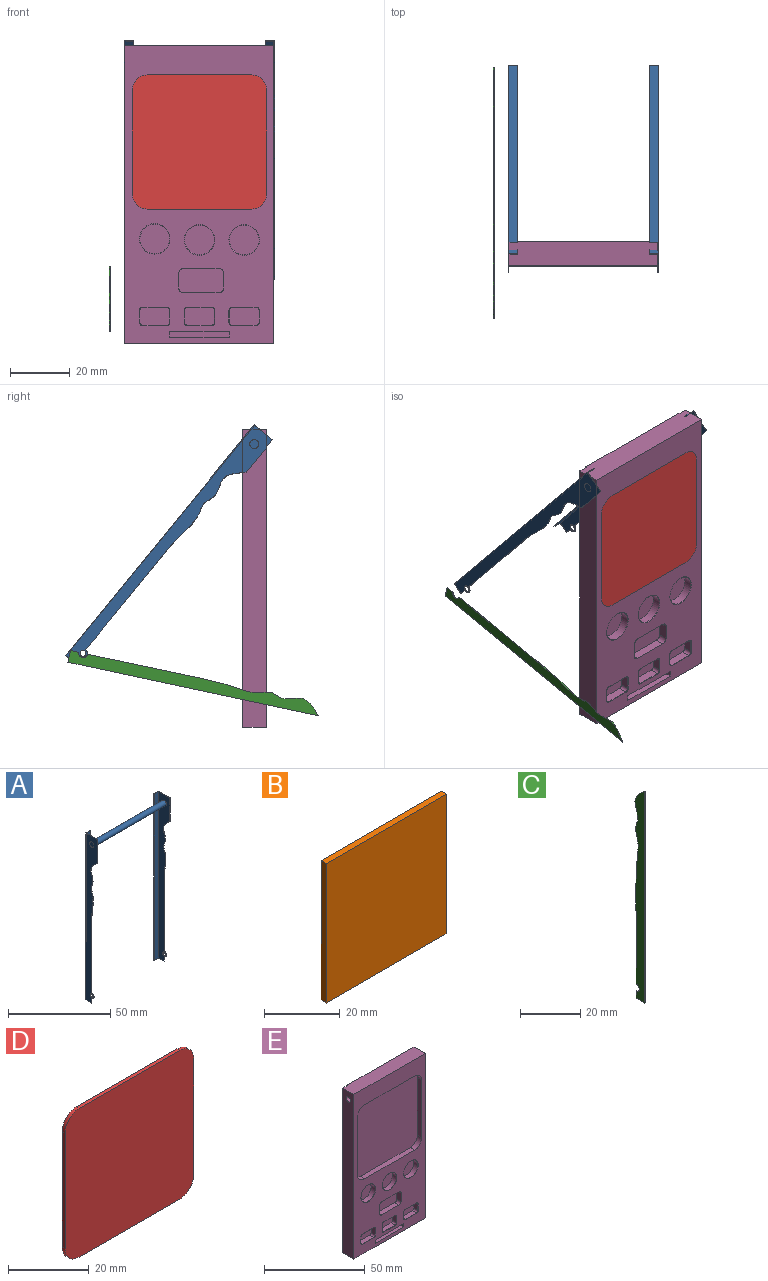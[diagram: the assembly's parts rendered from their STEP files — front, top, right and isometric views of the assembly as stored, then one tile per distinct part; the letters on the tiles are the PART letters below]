
ASSEMBLY  parts=5 mates=9
PART A: 27 faces, bbox 50.4x8x100 mm
  f0: plane 8.17x0.2mm, normal (0,-1,0), area 1.6mm2, adj f6,f8,f20,f25
  f1: plane 2.8x0.2mm, normal (0,-1,0), area 0.6mm2, adj f2,f4,f5,f23
  f2: plane 100x8mm, normal (-1,0,0), area 470.7mm2, adj f1,f3,f5,f11,f13,f21,f22,f23
  f3: plane 14.09x0.2mm, normal (0,-1,0), area 2.8mm2, adj f2,f4,f13,f21
  f4: plane 100x7.8mm, normal (1,0,0), area 443.7mm2, adj f1,f3,f5,f12,f13,f18,f21,f22
  f5: plane 4x3.2mm, normal (0,0,-1), area 1.4mm2, adj f1,f2,f4,f10,f11,f12
  f6: plane 100x7.8mm, normal (-1,0,0), area 443.7mm2, adj f0,f7,f9,f16,f17,f18,f19,f20
  f7: plane 14.09x0.2mm, normal (0,-1,0), area 2.8mm2, adj f6,f8,f17,f20
  f8: plane 100x8mm, normal (1,0,0), area 470.7mm2, adj f0,f7,f9,f14,f17,f19,f20,f25
  f9: plane 4x3.2mm, normal (0,0,-1), area 1.4mm2, adj f6,f8,f14,f15,f16,f19
  f10: plane 100x0.2mm, normal (1,0,0), area 20mm2, adj f5,f11,f12,f13
  f11: plane 100x3.2mm, normal (0,1,0), area 320mm2, adj f2,f5,f10,f13
  f12: plane 100x3mm, normal (0,-1,0), area 300mm2, adj f4,f5,f10,f13
  f13: plane 8x3.2mm, normal (0,0,1), area 2.2mm2, adj f2,f3,f4,f10,f11,f12
  f14: plane 100x3.2mm, normal (0,1,0), area 320mm2, adj f8,f9,f15,f17
  f15: plane 100x0.2mm, normal (-1,0,0), area 20mm2, adj f9,f14,f16,f17
  f16: plane 100x3mm, normal (0,-1,0), area 300mm2, adj f6,f9,f15,f17
  f17: plane 8x3.2mm, normal (0,0,1), area 2.2mm2, adj f6,f7,f8,f14,f15,f16
  f18: cylinder r=1.5mm len=50mm, axis (-1,0,0), area 471.2mm2, adj f4,f6
  f19: plane 2.8x0.2mm, normal (0,-1,0), area 0.6mm2, adj f6,f8,f9,f25
  f20: extruded ~71.94x4.46mm, area 14.8mm2, adj f0,f6,f7,f8
  f21: extruded ~71.94x4.46mm, area 14.8mm2, adj f2,f3,f4,f22
  f22: plane 8.17x0.2mm, normal (0,-1,0), area 1.6mm2, adj f2,f4,f21,f23
  f23: cylinder r=1.5mm len=3mm, axis (-1,0,0), area 0.9mm2, adj f1,f2,f4,f22
  f24: cylinder r=1mm len=2mm, axis (-1,0,0), area 1.3mm2, adj f2,f4
  f25: cylinder r=1.5mm len=3mm, axis (1,0,0), area 0.9mm2, adj f0,f6,f8,f19
  f26: cylinder r=1mm len=2mm, axis (1,0,0), area 1.3mm2, adj f6,f8
PART B: 6 faces, bbox 45x2x45 mm
  f0: plane 45x2mm, normal (0,0,1), area 90mm2, adj f1,f3,f4,f5
  f1: plane 45x2mm, normal (-1,0,0), area 90mm2, adj f0,f2,f4,f5
  f2: plane 45x2mm, normal (0,0,-1), area 90mm2, adj f1,f3,f4,f5
  f3: plane 45x2mm, normal (1,0,0), area 90mm2, adj f0,f2,f4,f5
  f4: plane 45x45mm, normal (0,-1,0), area 2025mm2, adj f0,f1,f2,f3
  f5: plane 45x45mm, normal (0,1,0), area 2025mm2, adj f0,f1,f2,f3
PART C: 8 faces, bbox 0.2x6.2x85.9 mm
  f0: plane 8.17x0.2mm, normal (0,1,0), area 1.6mm2, adj f2,f4,f5,f7
  f1: plane 4x0.2mm, normal (0,0,-1), area 0.8mm2, adj f2,f3,f4,f6
  f2: plane 85.91x6.23mm, normal (1,0,0), area 326.1mm2, adj f0,f1,f3,f5,f6,f7
  f3: plane 85.91x0.2mm, normal (0,-1,0), area 17.2mm2, adj f1,f2,f4,f5
  f4: plane 85.91x6.23mm, normal (-1,0,0), area 326.1mm2, adj f0,f1,f3,f5,f6,f7
  f5: extruded ~71.94x4.46mm, area 14.8mm2, adj f0,f2,f3,f4
  f6: plane 2.8x0.2mm, normal (0,1,0), area 0.6mm2, adj f1,f2,f4,f7
  f7: cylinder r=1.5mm len=3mm, axis (-1,0,0), area 0.9mm2, adj f0,f2,f4,f6
PART D: 10 faces, bbox 45x1x45 mm
  f0: plane 35x1mm, normal (0,0,1), area 35mm2, adj f4,f5,f6,f9
  f1: plane 35x1mm, normal (-1,0,0), area 35mm2, adj f4,f5,f6,f7
  f2: plane 35x1mm, normal (0,0,-1), area 35mm2, adj f4,f5,f7,f8
  f3: plane 35x1mm, normal (1,0,0), area 35mm2, adj f4,f5,f8,f9
  f4: plane 45x45mm, normal (0,-1,0), area 2003.5mm2, adj f0,f1,f2,f3,f6,f7,f8,f9
  f5: plane 45x45mm, normal (0,1,0), area 2003.5mm2, adj f0,f1,f2,f3,f6,f7,f8,f9
  f6: cylinder r=5mm len=5mm, axis (0,-1,0), area 7.9mm2, adj f0,f1,f4,f5
  f7: cylinder r=5mm len=5mm, axis (0,1,0), area 7.9mm2, adj f1,f2,f4,f5
  f8: cylinder r=5mm len=5mm, axis (0,-1,0), area 7.9mm2, adj f2,f3,f4,f5
  f9: cylinder r=5mm len=5mm, axis (0,1,0), area 7.9mm2, adj f0,f3,f4,f5
PART E: 102 faces, bbox 50x8x100 mm
  f0: plane 100x50mm, normal (0,-1,0), area 2406.6mm2, adj f1,f2,f4,f5,f6,f7,f8,f9
  f1: plane 50x8mm, normal (0,0,-1), area 338.8mm2, adj f0,f3,f4,f5,f85,f86,f87,f88
  f2: plane 50x8mm, normal (0,0,1), area 398.8mm2, adj f0,f3,f4,f5,f85,f86,f87,f88
  f3: plane 100x44mm, normal (0,1,0), area 2000mm2, adj f1,f2,f85,f88,f89,f90,f92
  f4: plane 100x7.8mm, normal (-1,0,0), area 772.9mm2, adj f0,f1,f2,f84,f87
  f5: plane 100x7.8mm, normal (1,0,0), area 772.9mm2, adj f0,f1,f2,f84,f86
  f6: plane 35x3mm, normal (0,0,-1), area 105mm2, adj f0,f10,f80,f83
  f7: plane 35x3mm, normal (1,0,0), area 105mm2, adj f0,f10,f80,f81
  f8: plane 35x3mm, normal (0,0,1), area 105mm2, adj f0,f10,f81,f82
  f9: plane 35x3mm, normal (-1,0,0), area 105mm2, adj f0,f10,f82,f83
  f10: plane 45x45mm, normal (0,-1,0), area 2003.5mm2, adj f6,f7,f8,f9,f80,f81,f82,f83
  f11: cylinder r=5mm len=10mm, axis (0,-1,0), area 91.1mm2, adj f12,f79
  f12: plane 10x10mm, normal (0,-1,0), area 78.5mm2, adj f11
  f13: plane 4x2.9mm, normal (1,0,0), area 11.6mm2, adj f14,f20,f21,f56
  f14: cylinder r=1mm len=2.9mm, axis (0,-1,0), area 4.6mm2, adj f13,f15,f21,f54
  f15: plane 8x2.9mm, normal (0,0,1), area 23.2mm2, adj f14,f16,f21,f53
  f16: cylinder r=1mm len=2.9mm, axis (0,-1,0), area 4.6mm2, adj f15,f17,f21,f55
  f17: plane 4x2.9mm, normal (-1,0,0), area 11.6mm2, adj f16,f18,f21,f57
  f18: cylinder r=1mm len=2.9mm, axis (0,-1,0), area 4.6mm2, adj f17,f19,f21,f59
  f19: plane 8x2.9mm, normal (0,0,-1), area 23.2mm2, adj f18,f20,f21,f60
  f20: cylinder r=1mm len=2.9mm, axis (0,-1,0), area 4.6mm2, adj f13,f19,f21,f58
  f21: plane 10x6mm, normal (0,-1,0), area 59.1mm2, adj f13,f14,f15,f16,f17,f18,f19,f20
  f22: plane 12x3mm, normal (0,0,1), area 36mm2, adj f0,f23,f29,f30
  f23: cylinder r=1.5mm len=3mm, axis (0,-1,0), area 7.1mm2, adj f0,f22,f24,f30
  f24: plane 5x3mm, normal (-1,0,0), area 15mm2, adj f0,f23,f25,f30
  f25: cylinder r=1.5mm len=3mm, axis (0,-1,0), area 7.1mm2, adj f0,f24,f26,f30
  f26: plane 12x3mm, normal (0,0,-1), area 36mm2, adj f0,f25,f27,f30
  f27: cylinder r=1.5mm len=3mm, axis (0,-1,0), area 7.1mm2, adj f0,f26,f28,f30
  f28: plane 5x3mm, normal (1,0,0), area 15mm2, adj f0,f27,f29,f30
  f29: cylinder r=1.5mm len=3mm, axis (0,-1,0), area 7.1mm2, adj f0,f22,f28,f30
  f30: plane 15x8mm, normal (0,-1,0), area 118.1mm2, adj f22,f23,f24,f25,f26,f27,f28,f29
  f31: plane 8x2.9mm, normal (0,0,1), area 23.2mm2, adj f32,f38,f39,f61
  f32: cylinder r=1mm len=2.9mm, axis (0,-1,0), area 4.6mm2, adj f31,f33,f39,f63
  f33: plane 4x2.9mm, normal (-1,0,0), area 11.6mm2, adj f32,f34,f39,f65
  f34: cylinder r=1mm len=2.9mm, axis (0,-1,0), area 4.6mm2, adj f33,f35,f39,f67
  f35: plane 8x2.9mm, normal (0,0,-1), area 23.2mm2, adj f34,f36,f39,f68
  f36: cylinder r=1mm len=2.9mm, axis (0,-1,0), area 4.6mm2, adj f35,f37,f39,f66
  f37: plane 4x2.9mm, normal (1,0,0), area 11.6mm2, adj f36,f38,f39,f64
  f38: cylinder r=1mm len=2.9mm, axis (0,-1,0), area 4.6mm2, adj f31,f37,f39,f62
  f39: plane 10x6mm, normal (0,-1,0), area 59.1mm2, adj f31,f32,f33,f34,f35,f36,f37,f38
  f40: plane 8x2.9mm, normal (0,0,1), area 23.2mm2, adj f41,f47,f48,f71
  f41: cylinder r=1mm len=2.9mm, axis (0,-1,0), area 4.6mm2, adj f40,f42,f48,f69
  f42: plane 4x2.9mm, normal (-1,0,0), area 11.6mm2, adj f41,f43,f48,f70
  f43: cylinder r=1mm len=2.9mm, axis (0,-1,0), area 4.6mm2, adj f42,f44,f48,f72
  f44: plane 8x2.9mm, normal (0,0,-1), area 23.2mm2, adj f43,f45,f48,f74
  f45: cylinder r=1mm len=2.9mm, axis (0,-1,0), area 4.6mm2, adj f44,f46,f48,f76
  f46: plane 4x2.9mm, normal (1,0,0), area 11.6mm2, adj f45,f47,f48,f75
  f47: cylinder r=1mm len=2.9mm, axis (0,-1,0), area 4.6mm2, adj f40,f46,f48,f73
  f48: plane 10x6mm, normal (0,-1,0), area 59.1mm2, adj f40,f41,f42,f43,f44,f45,f46,f47
  f49: cylinder r=5mm len=10mm, axis (0,-1,0), area 91.1mm2, adj f50,f77
  f50: plane 10x10mm, normal (0,-1,0), area 78.5mm2, adj f49
  f51: cylinder r=5mm len=10mm, axis (0,-1,0), area 91.1mm2, adj f52,f78
  f52: plane 10x10mm, normal (0,-1,0), area 78.5mm2, adj f51
  f53: plane 8x0.1mm, normal (0,-0.71,0.71), area 1.1mm2, adj f0,f15,f54,f55
  f54: cone r=1mm half-angle=45deg, axis (0,-1,0), area 0.2mm2, adj f0,f14,f53,f56
  f55: cone r=1mm half-angle=45deg, axis (0,-1,0), area 0.2mm2, adj f0,f16,f53,f57
  f56: plane 4x0.1mm, normal (0.71,-0.71,0), area 0.6mm2, adj f0,f13,f54,f58
  f57: plane 4x0.1mm, normal (-0.71,-0.71,0), area 0.6mm2, adj f0,f17,f55,f59
  f58: cone r=1mm half-angle=45deg, axis (0,-1,0), area 0.2mm2, adj f0,f20,f56,f60
  f59: cone r=1mm half-angle=45deg, axis (0,-1,0), area 0.2mm2, adj f0,f18,f57,f60
  f60: plane 8x0.1mm, normal (0,-0.71,-0.71), area 1.1mm2, adj f0,f19,f58,f59
  f61: plane 8x0.1mm, normal (0,-0.71,0.71), area 1.1mm2, adj f0,f31,f62,f63
  f62: cone r=1mm half-angle=45deg, axis (0,-1,0), area 0.2mm2, adj f0,f38,f61,f64
  f63: cone r=1mm half-angle=45deg, axis (0,-1,0), area 0.2mm2, adj f0,f32,f61,f65
  f64: plane 4x0.1mm, normal (0.71,-0.71,0), area 0.6mm2, adj f0,f37,f62,f66
  f65: plane 4x0.1mm, normal (-0.71,-0.71,0), area 0.6mm2, adj f0,f33,f63,f67
  f66: cone r=1mm half-angle=45deg, axis (0,-1,0), area 0.2mm2, adj f0,f36,f64,f68
  f67: cone r=1mm half-angle=45deg, axis (0,-1,0), area 0.2mm2, adj f0,f34,f65,f68
  f68: plane 8x0.1mm, normal (0,-0.71,-0.71), area 1.1mm2, adj f0,f35,f66,f67
  f69: cone r=1mm half-angle=45deg, axis (0,-1,0), area 0.2mm2, adj f0,f41,f70,f71
  f70: plane 4x0.1mm, normal (-0.71,-0.71,0), area 0.6mm2, adj f0,f42,f69,f72
  f71: plane 8x0.1mm, normal (0,-0.71,0.71), area 1.1mm2, adj f0,f40,f69,f73
  f72: cone r=1mm half-angle=45deg, axis (0,-1,0), area 0.2mm2, adj f0,f43,f70,f74
  f73: cone r=1mm half-angle=45deg, axis (0,-1,0), area 0.2mm2, adj f0,f47,f71,f75
  f74: plane 8x0.1mm, normal (0,-0.71,-0.71), area 1.1mm2, adj f0,f44,f72,f76
  f75: plane 4x0.1mm, normal (0.71,-0.71,0), area 0.6mm2, adj f0,f46,f73,f76
  f76: cone r=1mm half-angle=45deg, axis (0,-1,0), area 0.2mm2, adj f0,f45,f74,f75
  f77: cone r=5mm half-angle=45deg, axis (0,-1,0), area 4.5mm2, adj f0,f49
  f78: cone r=5mm half-angle=45deg, axis (0,-1,0), area 4.5mm2, adj f0,f51
  f79: cone r=5mm half-angle=45deg, axis (0,-1,0), area 4.5mm2, adj f0,f11
  f80: cylinder r=5mm len=5mm, axis (0,-1,0), area 23.6mm2, adj f0,f6,f7,f10
  f81: cylinder r=5mm len=5mm, axis (0,1,0), area 23.6mm2, adj f0,f7,f8,f10
  f82: cylinder r=5mm len=5mm, axis (0,-1,0), area 23.6mm2, adj f0,f8,f9,f10
  f83: cylinder r=5mm len=5mm, axis (0,1,0), area 23.6mm2, adj f0,f6,f9,f10
  f84: cylinder r=1.5mm len=50mm, axis (1,0,0), area 471.2mm2, adj f4,f5
  f85: plane 100x0.2mm, normal (1,0,0), area 20mm2, adj f1,f2,f3,f86
  f86: plane 100x3mm, normal (0,1,0), area 300mm2, adj f1,f2,f5,f85
  f87: plane 100x3mm, normal (0,1,0), area 300mm2, adj f1,f2,f4,f88
  f88: plane 100x0.2mm, normal (-1,0,0), area 20mm2, adj f1,f2,f3,f87
  f89: plane 80x2mm, normal (1,0,0), area 159.2mm2, adj f1,f3,f91,f92,f95
  f90: plane 80x2mm, normal (-1,0,0), area 159.2mm2, adj f1,f3,f91,f92,f94
  f91: plane 80x30mm, normal (0,1,0), area 2400mm2, adj f1,f89,f90,f92
  f92: plane 30x2mm, normal (0,0,-1), area 60mm2, adj f3,f89,f90,f91
  f93: plane 1x1mm, normal (-1,0,0), area 0.8mm2, adj f94
  f94: cylinder r=0.5mm len=3mm, axis (-1,0,0), area 9.4mm2, adj f90,f93
  f95: cylinder r=0.5mm len=3mm, axis (-1,0,0), area 9.4mm2, adj f89,f96
  f96: plane 1x1mm, normal (1,0,0), area 0.8mm2, adj f95
  f97: plane 20x4mm, normal (0,0,-1), area 80mm2, adj f0,f98,f100,f101
  f98: plane 4x2mm, normal (1,0,0), area 8mm2, adj f0,f97,f99,f101
  f99: plane 20x4mm, normal (0,0,1), area 80mm2, adj f0,f98,f100,f101
  f100: plane 4x2mm, normal (-1,0,0), area 8mm2, adj f0,f97,f99,f101
  f101: plane 20x2mm, normal (0,-1,0), area 40mm2, adj f97,f98,f99,f100
PLACE A rot(axis=(1,0,0),39.2deg) t=(0,61.07,18.95)mm
PLACE B at identity
PLACE C rot(axis=(1,0,0),102.1deg) t=(-5.01,66.49,21.81)mm
PLACE D at identity
PLACE E at identity fixed
MATE planar D.f0 <-> E.f6  axis (0,0,1) through (0,0.5,90)mm
MATE planar E.f8 <-> B.f2  axis (0,0,1) through (0,1.5,45)mm
MATE planar E.f9 <-> B.f3  axis (-1,0,0) through (22.5,1.5,67.5)mm
MATE cylindrical C.f7 <-> A.f23  axis (-1,0,0) through (-30.21,61.45,24.82)mm
MATE planar B.f4 <-> D.f5  axis (0,-1,0) through (0,1,67.5)mm
MATE planar E.f4 <-> A.f4  axis (-1,0,0) through (-25,3.9,49.59)mm
MATE cylindrical A.f18 <-> E.f84  axis (-1,0,0) through (0,4,95)mm
MATE planar D.f1 <-> E.f7  axis (-1,0,0) through (-22.5,0.5,67.5)mm
MATE planar E.f10 <-> B.f5  axis (0,-1,0) through (0,3,67.5)mm
